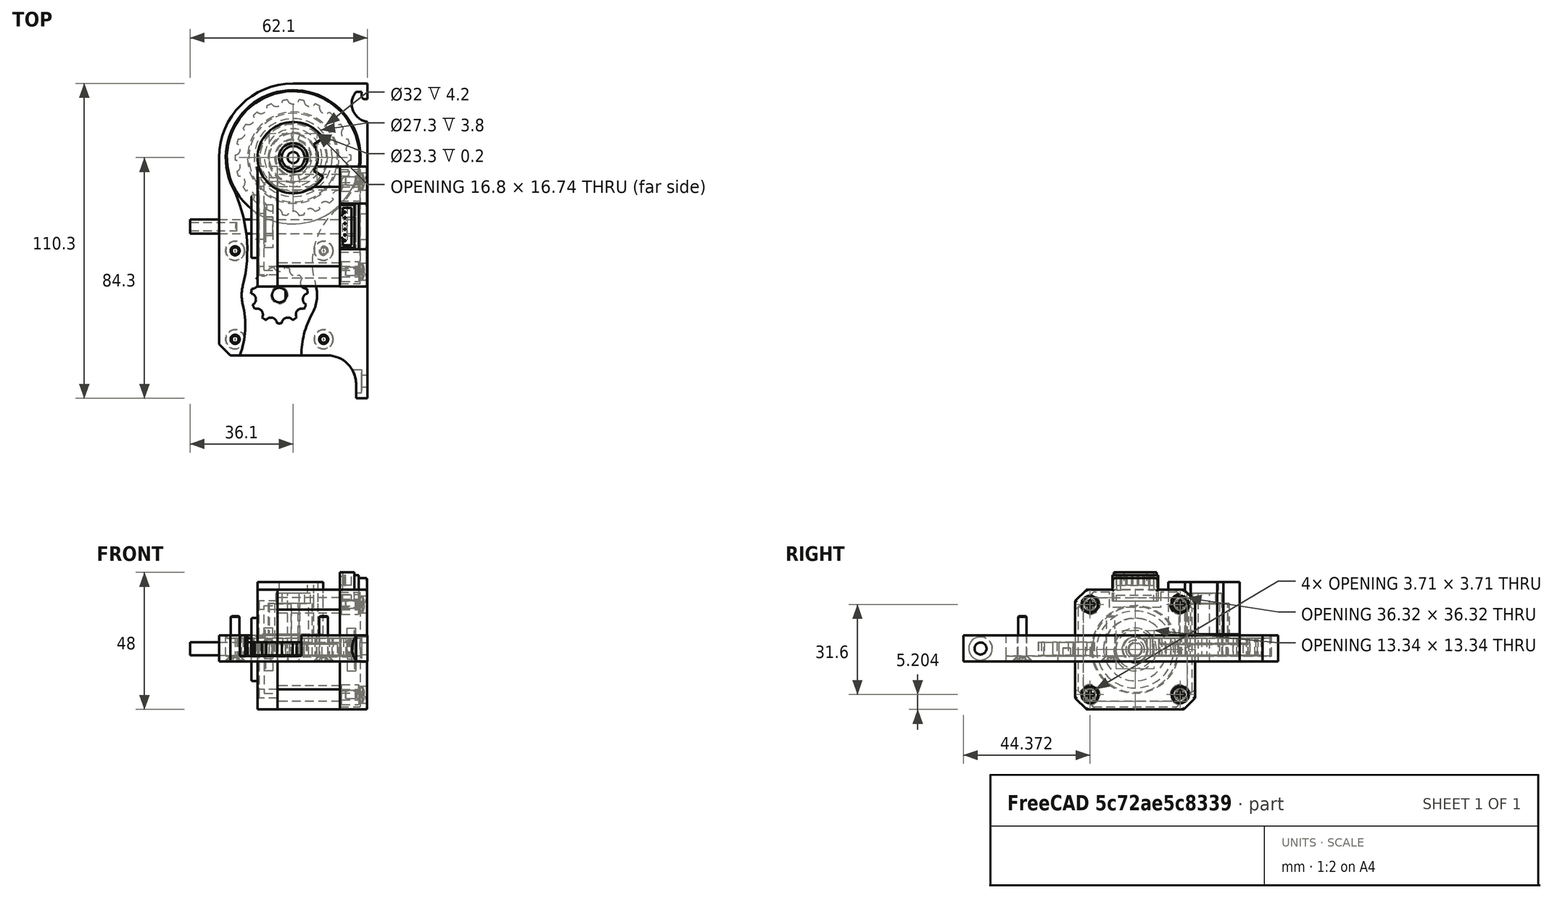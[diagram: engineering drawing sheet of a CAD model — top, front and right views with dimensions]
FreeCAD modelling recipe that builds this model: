
FCSTD DOCUMENT  (FreeCAD 0.19R24276 (Git))
Label: integrated-roller-clutch
License: All rights reserved
LicenseURL: http://en.wikipedia.org/wiki/All_rights_reserved
objects: Sketcher::SketchObject×27, Part::Feature×20, PartDesign::Pad×16, PartDesign::Pocket×11, PartDesign::Body×4, Part::FeaturePython×4, Spreadsheet::Sheet×2, PartDesign::PolarPattern×2, PartDesign::Hole×2, PartDesign::Chamfer×1, PartDesign::Fillet×1, Part::Compound2×1
note: 119 computed .brp shape members not serialized (recipe doc carries the construction recipe); baked Part::Feature solids carry a one-line shape summary decoded from their .brp

FEATURE [Spreadsheet::Sheet] Spreadsheet  label="Params"
  cells = A3=Chain Ball Spacing; B3(ChainBallSpacing)=5.95; A4=Chain Ball Diameter; B4(ChainBallDiameter)=4.2; A5=Chain String Diameter; B5(ChainStringDiameter)=1; A7=Cover Max Diameter; B7(CoverMaxDiameter)=46; A8=Cover Boom Diameter; B8(CoverBoomDiameter)=20; A11=Cover Pulley Teeths; B11(CoverPulleyTeeths)=22; A12=Motor Pulley Teeths; B12(MotorPulleyTeeths)=11
FEATURE [Sketcher::SketchObject] Sketch  label="Bracket Profile"
  FullyConstrained = false
  MapMode = 5
  Support = -> [XY_Plane]
  expr: Constraints[27] = <<Params>>.CoverBoomDiameter
  expr: Constraints[1] = <<Params>>.CoverMaxDiameter
  sketch-geometry (18):
    g0: Circle CenterX=0 CenterY=0 CenterZ=0 NormalX=0 NormalY=0 NormalZ=1 AngleXU=0 Radius=23
    g1: GeomPoint X=0 Y=23 Z=0
    g2: GeomPoint X=23 Y=0 Z=0
    g3: GeomPoint X=26 Y=26 Z=0
    g4: LineSegment StartX=26 StartY=26 StartZ=0 EndX=26 EndY=-84.3 EndZ=0
    g5: LineSegment StartX=26 StartY=-84.3 StartZ=0 EndX=22 EndY=-84.3 EndZ=0
    g6: LineSegment StartX=22 StartY=-84.3 StartZ=0 EndX=22 EndY=-79.3 EndZ=0
    g7: LineSegment StartX=12 StartY=-69.3 StartZ=0 EndX=-26 EndY=-69.3 EndZ=0
    g8: LineSegment StartX=-26 StartY=-69.3 StartZ=0 EndX=-26 EndY=26 EndZ=0
    g9: LineSegment StartX=-26 StartY=26 StartZ=0 EndX=26 EndY=26 EndZ=0
    g10: GeomPoint X=-23 Y=0 Z=0
    g11: GeomPoint X=0 Y=-23 Z=0
    g12: ArcOfCircle CenterX=12 CenterY=-79.3 CenterZ=0 NormalX=0 NormalY=0 NormalZ=1 AngleXU=0 Radius=10 StartAngle=0 EndAngle=1.5708
    g13: LineSegment StartX=16.3 StartY=-69.3 StartZ=0 EndX=16.3 EndY=-27 EndZ=0
    g14: LineSegment StartX=16.3 StartY=-27 StartZ=0 EndX=-26 EndY=-27 EndZ=0
    g15: LineSegment StartX=-26 StartY=-27 StartZ=0 EndX=-26 EndY=-69.3 EndZ=0
    g16: LineSegment StartX=-26 StartY=-69.3 StartZ=0 EndX=16.3 EndY=-69.3 EndZ=0
    g17: Circle CenterX=-4.85 CenterY=-48.15 CenterZ=0 NormalX=0 NormalY=0 NormalZ=1 AngleXU=0 Radius=29.9106
  constraints (46):
    c: Coincident(g0,g-1)
    c: Diameter(g0) = 46
    c: PointOnObject(g1,g-2)
    c: PointOnObject(g1,g0)
    c: PointOnObject(g2,g0)
    c: PointOnObject(g2,g-1)
    c: DistanceY(g1,g3) = 3
    c: DistanceX(g2,g3) = 3
    c: Coincident(g4,g3)
    c: Vertical(g4)
    c: Coincident(g4,g5)
    c: Horizontal(g5)
    c: Coincident(g5,g6)
    c: Vertical(g6)
    c: Coincident(g7,g8)
    c: Vertical(g8)
    c: Coincident(g8,g9)
    c: Coincident(g9,g3)
    c: Horizontal(g9)
    c: Horizontal(g7,g7)
    c: Distance(g5) = 4
    c: Distance(g6) = 5
    c: PointOnObject(g10,g0)
    c: PointOnObject(g11,g0)
    c: PointOnObject(g11,g-2)
    c: PointOnObject(g10,g-1)
    c: DistanceX(g8,g10) = 3
    c: Diameter(g12) = 20
    c: Angle(g12) = 1.5708
    c: Tangent(g12,g6) = -1.5708
    c: Coincident(g7,g12)
    c: Coincident(g13,g14)
    c: Coincident(g14,g15)
    c: Coincident(g15,g16)
    c: Coincident(g16,g13)
    c: Equal(g13,g14)
    c: Equal(g13,g15)
    c: Equal(g13,g16)
    c: PointOnObject(g13,g17)
    c: PointOnObject(g14,g17)
    c: PointOnObject(g15,g17)
    c: PointOnObject(g16,g17)
    c: Distance(g16) = 42.3
    c: Angle(g16) = 0
    c: Coincident(g15,g7)
    c: DistanceY(g13,g11) = 4
FEATURE [PartDesign::Pad] Pad  label="Bracket Body"
  AllowMultiFace = false
  Direction = (1,1,1)
  Length = 2
  Length2 = 100
  Profile = -> Sketch
  Type = 0
FEATURE [Sketcher::SketchObject] Sketch001  label="Bearing Cup Profile"
  FullyConstrained = true
  MapMode = 5
  Placement = pos=(0,0,2) rot=(0,0,1;0rad)
  Support = -> [Pad]
  expr: Constraints[0] = Spreadsheet001.MainCoverBearingOuterDiameter + 0.3
  expr: Constraints[1] = Spreadsheet001.MainCoverBearingOuterDiameter + 4
  sketch-geometry (2):
    g0: Circle CenterX=0 CenterY=0 CenterZ=0 NormalX=0 NormalY=0 NormalZ=1 AngleXU=0 Radius=13.65
    g1: Circle CenterX=0 CenterY=0 CenterZ=0 NormalX=0 NormalY=0 NormalZ=1 AngleXU=0 Radius=15.5
  constraints (4):
    c: Diameter(g0) = 27.3
    c: Diameter(g1) = 31
    c: Coincident(g1,g0)
    c: Coincident(g1,g-1)
FEATURE [PartDesign::Pad] Pad001  label="Main Bearing Cup"
  AllowMultiFace = false
  BaseFeature = -> Pad
  Direction = (1,1,1)
  Length = 4
  Length2 = 100
  Profile = -> Sketch001
  Type = 0
  expr: Length = Spreadsheet001.CoverBearingWidth
FEATURE [Sketcher::SketchObject] Sketch002  label="Bearing Shim Profile"
  ExternalGeometry = -> [Pad001]
  FullyConstrained = true
  MapMode = 5
  Placement = pos=(0,0,2) rot=(0,0,1;0rad)
  Support = -> [Pad001]
  sketch-geometry (4):
    g0: GeomPoint X=-13.65 Y=0 Z=0
    g1: GeomPoint X=-11.65 Y=0 Z=0
    g2: Circle CenterX=0 CenterY=0 CenterZ=0 NormalX=0 NormalY=0 NormalZ=1 AngleXU=0 Radius=11.65
    g3: Circle CenterX=0 CenterY=0 CenterZ=0 NormalX=0 NormalY=0 NormalZ=1 AngleXU=0 Radius=13.65
  constraints (8):
    c: PointOnObject(g0,g-1)
    c: PointOnObject(g0,g-3)
    c: PointOnObject(g1,g-1)
    c: Coincident(g2,g-1)
    c: PointOnObject(g1,g2)
    c: Coincident(g3,g2)
    c: PointOnObject(g0,g3)
    c: Distance(g0,g1) = 2
FEATURE [PartDesign::Pad] Pad002  label="Main Bearing Shim"
  AllowMultiFace = false
  BaseFeature = -> Pad001
  Direction = (1,1,1)
  Length = 0.2
  Length2 = 100
  Profile = -> Sketch002
  Type = 0
FEATURE [Sketcher::SketchObject] Sketch003  label="Spring Shim Profile"
  FullyConstrained = true
  MapMode = 5
  Placement = pos=(0,0,2) rot=(0,0,1;0rad)
  Support = -> [Pad002]
  sketch-geometry (1):
    g0: Circle CenterX=0 CenterY=0 CenterZ=0 NormalX=0 NormalY=0 NormalZ=1 AngleXU=0 Radius=6.1
  constraints (2):
    c: Coincident(g0,g-1)
    c: Diameter(g0) = 12.2
FEATURE [PartDesign::Pad] Pad003  label="Spring Shim"
  AllowMultiFace = false
  BaseFeature = -> Pad002
  Direction = (1,1,1)
  Length = 0.2
  Length2 = 100
  Profile = -> Sketch003
  Type = 0
FEATURE [Sketcher::SketchObject] Sketch004  label="Spring Stud Profile"
  FullyConstrained = true
  MapMode = 5
  Placement = pos=(0,0,2.2) rot=(0,0,1;0rad)
  Support = -> [Pad003]
  sketch-geometry (1):
    g0: Circle CenterX=0 CenterY=0 CenterZ=0 NormalX=0 NormalY=0 NormalZ=1 AngleXU=0 Radius=5.4
  constraints (2):
    c: Coincident(g0,g-1)
    c: Diameter(g0) = 10.8
FEATURE [PartDesign::Pad] Pad004  label="Spring Stud"
  AllowMultiFace = false
  BaseFeature = -> Pad003
  Direction = (1,1,1)
  Length = 18.2
  Length2 = 100
  Profile = -> Sketch004
  Type = 0
FEATURE [Sketcher::SketchObject] Sketch005  label="Adapter Bearing Profile"
  FullyConstrained = true
  MapMode = 5
  Placement = pos=(0,0,20.4) rot=(0,0,1;0rad)
  Support = -> [Pad004]
  expr: Constraints[1] = <<StockParts>>.AdapterBearingInnerDiameter
  sketch-geometry (1):
    g0: Circle CenterX=0 CenterY=0 CenterZ=0 NormalX=0 NormalY=0 NormalZ=1 AngleXU=0 Radius=4
  constraints (2):
    c: Coincident(g0,g-1)
    c: Diameter(g0) = 8
FEATURE [PartDesign::Pad] Pad005  label="Adapter Bearing Stud"
  AllowMultiFace = false
  BaseFeature = -> Pad004
  Direction = (1,1,1)
  Length = 3.5
  Length2 = 100
  Profile = -> Sketch005
  Type = 0
  expr: Length = <<StockParts>>.AdapterBearingWidth
FEATURE [Sketcher::SketchObject] Sketch006  label="Pulley Base Profile"
  FullyConstrained = false
  MapMode = 5
  Support = -> [XY_Plane001]
  expr: Constraints[0] = <<Params>>.CoverPulleyTeeths * <<Params>>.ChainBallSpacing / pi - <<Params>>.ChainStringDiameter
  sketch-geometry (1):
    g0: Circle CenterX=0 CenterY=0 CenterZ=0 NormalX=0 NormalY=0 NormalZ=1 AngleXU=0 Radius=20.3334
  constraints (2):
    c: Diameter(g0) = 40.6668
    c: Coincident(g0,g-1)
FEATURE [PartDesign::Pad] Pad006  label="Pulley Body"
  AllowMultiFace = false
  Direction = (1,1,1)
  Length = 6
  Length2 = 100
  Profile = -> Sketch006
  Type = 0
FEATURE [Sketcher::SketchObject] Sketch007  label="Chain Ball Profile"
  FullyConstrained = false
  MapMode = 5
  Placement = pos=(0,0,6) rot=(0,0,1;0rad)
  Support = -> [Pad006]
  expr: Constraints[1] = <<Params>>.CoverPulleyTeeths * <<Params>>.ChainBallSpacing / pi / 2
  expr: Constraints[2] = <<Params>>.ChainBallDiameter
  sketch-geometry (1):
    g0: Circle CenterX=0 CenterY=20.8334 CenterZ=0 NormalX=0 NormalY=0 NormalZ=1 AngleXU=0 Radius=2.1
  constraints (3):
    c: PointOnObject(g0,g-2)
    c: Distance(g-1,g0) = 20.8334
    c: Diameter(g0) = 4.2
FEATURE [PartDesign::Pocket] Pocket  label="Single Teeth Cutout"
  AllowMultiFace = false
  BaseFeature = -> Pad006
  Length = 5
  Length2 = 100
  Profile = -> Sketch007
  Type = 1
FEATURE [PartDesign::PolarPattern] PolarPattern  label="All Teeth Cutout"
  Angle = 360
  Axis = -> Sketch007 [N_Axis]
  BaseFeature = -> Pocket
  Occurrences = 22
  Originals = -> [Pocket]
  expr: Occurrences = <<Params>>.CoverPulleyTeeths
FEATURE [Sketcher::SketchObject] Sketch008  label="Bearing Profile"
  FullyConstrained = true
  MapMode = 5
  Placement = pos=(0,0,0) rot=(1,0,0;3.14159rad)
  Support = -> [PolarPattern]
  expr: Constraints[3] = <<StockParts>>.MainCoverBearingInnerDiameter + 0.15
  expr: Constraints[1] = <<StockParts>>.MainCoverBearingOuterDiameter + 4 + 1
  sketch-geometry (2):
    g0: Circle CenterX=0 CenterY=0 CenterZ=0 NormalX=0 NormalY=0 NormalZ=1 AngleXU=0 Radius=16
    g1: Circle CenterX=0 CenterY=0 CenterZ=0 NormalX=0 NormalY=0 NormalZ=1 AngleXU=0 Radius=10.075
  constraints (4):
    c: Coincident(g0,g-1)
    c: Diameter(g0) = 32
    c: Coincident(g1,g0)
    c: Diameter(g1) = 20.15
FEATURE [Spreadsheet::Sheet] Spreadsheet001  label="StockParts"
  cells = A5=Cover Bearing Width; B5(CoverBearingWidth)=4; A6=Cover Outer Diameter; B6(MainCoverBearingOuterDiameter)=27; A7=Cover Inner Diameter; B7(MainCoverBearingInnerDiameter)=20; A10=Adapter Bearing Width; B10(AdapterBearingWidth)=3.5; A11=Adapter Bearing Outer Diameter; B11(AdapterBearingOuterDiameter)=12; A12=Adapter Bearing Inner Diameter; B12(AdapterBearingInnerDiameter)=8
FEATURE [Sketcher::SketchObject] Sketch013
  FullyConstrained = false
  MapMode = 5
  Placement = pos=(0,0,6) rot=(0,0,1;0rad)
  Support = -> [PolarPattern]
  expr: Constraints[1] = <<Params>>.ChainBallSpacing * <<Params>>.CoverPulleyTeeths / pi + <<Params>>.ChainBallDiameter + 1 - 0.4
  sketch-geometry (1):
    g0: Circle CenterX=0 CenterY=0 CenterZ=0 NormalX=0 NormalY=0 NormalZ=1 AngleXU=0 Radius=23.2334
  constraints (2):
    c: Coincident(g0,g-1)
    c: Diameter(g0) = 46.4668
FEATURE [PartDesign::Pad] Pad007
  AllowMultiFace = false
  BaseFeature = -> PolarPattern
  Direction = (1,1,1)
  Length = 1
  Length2 = 100
  Profile = -> Sketch013
  Type = 0
FEATURE [PartDesign::Pocket] Pocket001
  AllowMultiFace = false
  BaseFeature = -> Pad007
  Length = 4.2
  Length2 = 100
  Profile = -> Sketch008
  Type = 0
  expr: Length = Spreadsheet001.CoverBearingWidth + 0.2
FEATURE [Sketcher::SketchObject] Sketch014
  FullyConstrained = true
  MapMode = 5
  Placement = pos=(0,0,4.2) rot=(1,0,0;3.14159rad)
  Support = -> [Pocket001]
  expr: Constraints[1] = <<StockParts>>.MainCoverBearingInnerDiameter + 4
  sketch-geometry (1):
    g0: Circle CenterX=0 CenterY=0 CenterZ=0 NormalX=0 NormalY=0 NormalZ=1 AngleXU=0 Radius=12
  constraints (2):
    c: Coincident(g0,g-1)
    c: Diameter(g0) = 24
FEATURE [PartDesign::Pad] Pad008
  AllowMultiFace = false
  BaseFeature = -> Pocket001
  Direction = (1,1,1)
  Length = 0.2
  Length2 = 100
  Profile = -> Sketch014
  Type = 0
FEATURE [Sketcher::SketchObject] Sketch015
  FullyConstrained = true
  MapMode = 5
  Placement = pos=(0,0,0) rot=(1,0,0;3.14159rad)
  Support = -> [Pad008]
  sketch-geometry (1):
    g0: Circle CenterX=0 CenterY=0 CenterZ=0 NormalX=0 NormalY=0 NormalZ=1 AngleXU=0 Radius=8.4
  constraints (2):
    c: Coincident(g0,g-1)
    c: Diameter(g0) = 16.8
FEATURE [PartDesign::Pocket] Pocket002
  AllowMultiFace = false
  BaseFeature = -> Pad008
  Length = 5
  Length2 = 100
  Profile = -> Sketch015
  Type = 1
FEATURE [Sketcher::SketchObject] Sketch016
  ExternalGeometry = -> [Pocket002]
  FullyConstrained = true
  MapMode = 5
  Placement = pos=(0,0,0) rot=(1,0,0;3.14159rad)
  Support = -> [Pocket002]
  sketch-geometry (7):
    g0: GeomPoint X=8.4 Y=0 Z=0
    g1: LineSegment StartX=-0.732108 StartY=-8.36804 StartZ=0 EndX=-0.566512 EndY=-6.47527 EndZ=0
    g2: LineSegment StartX=-0.732108 StartY=8.36804 StartZ=0 EndX=-0.566512 EndY=6.47527 EndZ=0
    g3: LineSegment StartX=-0.732108 StartY=8.36804 StartZ=0 EndX=8.4 EndY=0 EndZ=0
    g4: LineSegment StartX=8.4 StartY=0 StartZ=0 EndX=-0.732108 EndY=-8.36804 EndZ=0
    g5: ArcOfCircle CenterX=0 CenterY=0 CenterZ=0 NormalX=0 NormalY=0 NormalZ=1 AngleXU=0 Radius=8.4 StartAngle=1.65806 EndAngle=4.62512
    g6: ArcOfCircle CenterX=0 CenterY=0 CenterZ=0 NormalX=0 NormalY=0 NormalZ=1 AngleXU=0 Radius=6.5 StartAngle=1.65806 EndAngle=4.62512
  constraints (18):
    c: PointOnObject(g0,g-1)
    c: PointOnObject(g1,g-3)
    c: Coincident(g3,g2)
    c: Coincident(g3,g0)
    c: Coincident(g4,g0)
    c: Coincident(g4,g1)
    c: Equal(g4,g3)
    c: Coincident(g5,g-1)
    c: Coincident(g5,g2)
    c: Coincident(g5,g1)
    c: Coincident(g6,g5)
    c: Coincident(g6,g1)
    c: Coincident(g6,g2)
    c: Perpendicular(g6,g2)
    c: Perpendicular(g5,g1)
    c: Diameter(g6) = 13
    c: Angle(g6) = 2.96706
    c: PointOnObject(g0,g-3)
FEATURE [PartDesign::Pad] Pad009
  AllowMultiFace = false
  BaseFeature = -> Pocket002
  Direction = (1,1,1)
  Length = 18
  Length2 = 100
  Profile = -> Sketch016
  Reversed = true
  Type = 0
FEATURE [PartDesign::Body] Body001  label="Cover Pulley"
  Group = -> [Sketch006,Pad006,Sketch007,Pocket,PolarPattern,Sketch008,Sketch013,Pad007,Pocket001,Sketch014,Pad008,Sketch015,Pocket002,Sketch016,Pad009]
  Origin = -> Origin001
  Placement = pos=(0,0,2.2) rot=(0,0,1;0rad)
  Tip = -> Pad009
FEATURE [Sketcher::SketchObject] Sketch024
  FullyConstrained = false
  MapMode = 5
  Support = -> [XY_Plane004]
  expr: Constraints[1] = <<Params>>.ChainBallSpacing * <<Params>>.MotorPulleyTeeths / pi - <<Params>>.ChainStringDiameter
  sketch-geometry (1):
    g0: Circle CenterX=0 CenterY=0 CenterZ=0 NormalX=0 NormalY=0 NormalZ=1 AngleXU=0 Radius=9.91669
  constraints (2):
    c: Coincident(g0,g-1)
    c: Diameter(g0) = 19.8334
FEATURE [PartDesign::Pad] Pad016
  AllowMultiFace = false
  Direction = (1,1,1)
  Length = 4.6
  Length2 = 100
  Profile = -> Sketch024
  Type = 0
FEATURE [Sketcher::SketchObject] Sketch025
  FullyConstrained = false
  MapMode = 5
  Placement = pos=(0,0,4.6) rot=(0,0,1;0rad)
  Support = -> [Pad016]
  expr: Constraints[1] = <<Params>>.ChainBallDiameter
  expr: Constraints[2] = <<Params>>.ChainBallSpacing * <<Params>>.MotorPulleyTeeths / pi / 2
  sketch-geometry (1):
    g0: Circle CenterX=0 CenterY=10.4167 CenterZ=0 NormalX=0 NormalY=0 NormalZ=1 AngleXU=0 Radius=2.1
  constraints (3):
    c: PointOnObject(g0,g-2)
    c: Diameter(g0) = 4.2
    c: Distance(g-1,g0) = 10.4167
FEATURE [PartDesign::Pocket] Pocket004
  AllowMultiFace = false
  BaseFeature = -> Pad016
  Length = 5
  Length2 = 100
  Profile = -> Sketch025
  Type = 1
FEATURE [PartDesign::PolarPattern] PolarPattern001
  Angle = 360
  Axis = -> Sketch025 [N_Axis]
  BaseFeature = -> Pocket004
  Occurrences = 11
  Originals = -> [Pocket004]
  expr: Occurrences = <<Params>>.MotorPulleyTeeths
FEATURE [Sketcher::SketchObject] Sketch026
  FullyConstrained = false
  MapMode = 5
  Placement = pos=(0,0,4.6) rot=(0,0,1;0rad)
  Support = -> [PolarPattern001]
  sketch-geometry (2):
    g0: ArcOfCircle CenterX=0 CenterY=0 CenterZ=0 NormalX=0 NormalY=0 NormalZ=1 AngleXU=0 Radius=2.55 StartAngle=0.567705 EndAngle=5.71548
    g1: LineSegment StartX=2.15 StartY=-1.37113 StartZ=0 EndX=2.15 EndY=1.37113 EndZ=0
  constraints (6):
    c: Coincident(g0,g-1)
    c: Vertical(g0,g0)
    c: Coincident(g1,g0)
    c: Coincident(g1,g0)
    c: DistanceX(g0,g0) = 2.15
    c: Diameter(g0) = 5.1
FEATURE [PartDesign::Pocket] Pocket005
  AllowMultiFace = false
  BaseFeature = -> PolarPattern001
  Length = 5
  Length2 = 100
  Profile = -> Sketch026
  Type = 1
FEATURE [PartDesign::Pad] Pad018  label="Chain Compartment"
  AllowMultiFace = false
  BaseFeature = -> Pad005
  Direction = (1,1,1)
  Length = 7.2
  Length2 = 100
  Profile = -> Pad005 [Face5]
  Type = 0
FEATURE [Sketcher::SketchObject] Sketch034
  ExternalGeometry = -> [Pad018]
  FullyConstrained = true
  MapMode = 5
  Placement = pos=(0,0,9.2) rot=(0,0,1;0rad)
  Support = -> [Pad018]
  sketch-geometry (1):
    g0: Circle CenterX=-4.85 CenterY=-48.15 CenterZ=0 NormalX=0 NormalY=0 NormalZ=1 AngleXU=0 Radius=3
  constraints (3):
    c: Diameter(g0) = 6
    c: DistanceX(g-3,g0) = 21.15
    c: DistanceY(g-3,g0) = 21.15
FEATURE [PartDesign::Pocket] Pocket010  label="Shaft Hole"
  AllowMultiFace = false
  BaseFeature = -> Pad018
  Length = 5
  Length2 = 100
  Profile = -> Sketch034
  Type = 1
FEATURE [Sketcher::SketchObject] Sketch035
  ExternalGeometry = -> [Pocket010]
  FullyConstrained = true
  MapMode = 5
  Placement = pos=(0,0,0) rot=(1,0,0;3.14159rad)
  Support = -> [Pocket010]
  sketch-geometry (9):
    g0: LineSegment StartX=10.65 StartY=32.65 StartZ=0 EndX=10.65 EndY=63.65 EndZ=0
    g1: LineSegment StartX=10.65 StartY=63.65 StartZ=0 EndX=-20.35 EndY=63.65 EndZ=0
    g2: LineSegment StartX=-20.35 StartY=63.65 StartZ=0 EndX=-20.35 EndY=32.65 EndZ=0
    g3: LineSegment StartX=-20.35 StartY=32.65 StartZ=0 EndX=10.65 EndY=32.65 EndZ=0
    g4: Circle CenterX=-4.85 CenterY=48.15 CenterZ=0 NormalX=0 NormalY=0 NormalZ=1 AngleXU=0 Radius=21.9203
    g5: Circle CenterX=-20.35 CenterY=63.65 CenterZ=0 NormalX=0 NormalY=0 NormalZ=1 AngleXU=0 Radius=1.6
    g6: Circle CenterX=-20.35 CenterY=32.65 CenterZ=0 NormalX=0 NormalY=0 NormalZ=1 AngleXU=0 Radius=1.6
    g7: Circle CenterX=10.65 CenterY=32.65 CenterZ=0 NormalX=0 NormalY=0 NormalZ=1 AngleXU=0 Radius=1.6
    g8: Circle CenterX=10.65 CenterY=63.65 CenterZ=0 NormalX=0 NormalY=0 NormalZ=1 AngleXU=0 Radius=1.6
  constraints (22):
    c: Coincident(g0,g1)
    c: Coincident(g1,g2)
    c: Coincident(g2,g3)
    c: Coincident(g3,g0)
    c: Equal(g0,g1)
    c: Equal(g0,g2)
    c: Equal(g0,g3)
    c: PointOnObject(g0,g4)
    c: PointOnObject(g1,g4)
    c: PointOnObject(g2,g4)
    c: PointOnObject(g3,g4)
    c: Coincident(g4,g-3)
    c: Distance(g0) = 31
    c: Angle(g-1,g3) = 0
    c: Coincident(g5,g1)
    c: Coincident(g6,g2)
    c: Coincident(g7,g0)
    c: Coincident(g8,g0)
    c: Equal(g8,g5)
    c: Equal(g5,g6)
    c: Equal(g6,g7)
    c: Diameter(g8) = 3.2
FEATURE [PartDesign::Hole] Hole  label="Motor Mounting Screws"
  AllowMultiFace = false
  BaseFeature = -> Pocket010
  Depth = 25
  DepthType = 0
  Diameter = 3.2
  DrillForDepth = false
  DrillPoint = 1
  DrillPointAngle = 118
  HoleCutCountersinkAngle = 90
  HoleCutCustomValues = false
  HoleCutDepth = 0
  HoleCutDiameter = 6.8
  HoleCutType = 2
  ModelActualThread = false
  Profile = -> Sketch035
  Tapered = false
  TaperedAngle = 90
  ThreadAngle = 0
  ThreadClass = 0
  ThreadCutOffInner = 0
  ThreadCutOffOuter = 0
  ThreadDirection = 0
  ThreadFit = 0
  ThreadPitch = 0
  ThreadSize = 0
  ThreadType = 0
  Threaded = false
FEATURE [Sketcher::SketchObject] Sketch036
  ExternalGeometry = -> [Hole]
  FullyConstrained = true
  MapMode = 5
  Placement = pos=(0,0,9.2) rot=(0,0,1;0rad)
  Support = -> [Hole]
  expr: Constraints[16] = <<Params>>.ChainBallSpacing * <<Params>>.MotorPulleyTeeths / pi + <<Params>>.ChainBallDiameter + 1.4
  expr: Constraints[25] = <<Params>>.ChainBallSpacing * <<Params>>.CoverPulleyTeeths / pi + <<Params>>.ChainBallDiameter + 1.4
  sketch-geometry (11):
    g0: Circle CenterX=0 CenterY=0 CenterZ=0 NormalX=0 NormalY=0 NormalZ=1 AngleXU=0 Radius=15.5
    g1: ArcOfCircle CenterX=-66.09 CenterY=-32.4652 CenterZ=0 NormalX=0 NormalY=0 NormalZ=1 AngleXU=0 Radius=50 StartAngle=6.03245 EndAngle=6.73979
    g2: ArcOfCircle CenterX=31.6746 CenterY=-36.9043 CenterZ=0 NormalX=0 NormalY=0 NormalZ=1 AngleXU=0 Radius=25 StartAngle=2.28008 EndAngle=3.44028
    g3: GeomPoint X=-18.7 Y=-69.3 Z=0
    g4: GeomPoint X=7 Y=-69.3 Z=0
    g5: ArcOfCircle CenterX=-46.7615 CenterY=-58.6909 CenterZ=0 NormalX=0 NormalY=0 NormalZ=1 AngleXU=0 Radius=30 StartAngle=5.92173 EndAngle=6.52958
    g6: ArcOfCircle CenterX=32.8377 CenterY=-69.3 CenterZ=0 NormalX=0 NormalY=0 NormalZ=1 AngleXU=0 Radius=30 StartAngle=2.6302 EndAngle=3.14159
    g7: LineSegment StartX=-18.7 StartY=-69.3 StartZ=0 EndX=2.83766 EndY=-69.3 EndZ=0
    g8: ArcOfCircle CenterX=-4.85 CenterY=-48.15 CenterZ=0 NormalX=0 NormalY=0 NormalZ=1 AngleXU=0 Radius=13.2167 StartAngle=2.89086 EndAngle=3.38799
    g9: ArcOfCircle CenterX=-4.85 CenterY=-48.15 CenterZ=0 NormalX=0 NormalY=0 NormalZ=1 AngleXU=0 Radius=13.2167 StartAngle=5.77179 EndAngle=6.58187
    g10: ArcOfCircle CenterX=0 CenterY=0 CenterZ=0 NormalX=0 NormalY=0 NormalZ=1 AngleXU=0 Radius=23.6334 StartAngle=5.42168 EndAngle=9.88138
  constraints (27):
    c: Equal(g0,g-3)
    c: Coincident(g0,g-1)
    c: Radius(g2) = 25
    c: Radius(g1) = 50
    c: PointOnObject(g3,g-5)
    c: PointOnObject(g4,g-5)
    c: Distance(g3,g-5) = 7.3
    c: Distance(g4,g-5) = 5
    c: PointOnObject(g6,g-5)
    c: Perpendicular(g6,g-5)
    c: Radius(g5) = 30
    c: Radius(g6) = 30
    c: Coincident(g7,g5)
    c: Coincident(g7,g6)
    c: Coincident(g3,g5)
    c: Coincident(g9,g8)
    c: Diameter(g9) = 26.4334
    c: Equal(g9,g8)
    c: Tangent(g9,g6) = 1.5708
    c: Tangent(g9,g2) = 1.5708
    c: Tangent(g5,g8) = 1.5708
    c: Tangent(g8,g1) = 1.5708
    c: Coincident(g10,g0)
    c: Tangent(g1,g10) = 1.5708
    c: Tangent(g2,g10) = 1.5708
    c: Diameter(g10) = 47.2668
    c: Coincident(g-4,g8)
FEATURE [PartDesign::Pocket] Pocket011  label="Chain Guide"
  AllowMultiFace = false
  BaseFeature = -> Hole
  Length = 0
  Length2 = 100
  Profile = -> Sketch036
  Type = 3
  UpToFace = -> Hole [Face31]
FEATURE [Sketcher::SketchObject] Sketch037
  ExternalGeometry = -> [Pocket005]
  FullyConstrained = false
  MapMode = 5
  Placement = pos=(0,0,4.6) rot=(0,0,1;0rad)
  Support = -> [Pocket005]
  sketch-geometry (1):
    g0: Circle CenterX=0 CenterY=0 CenterZ=0 NormalX=0 NormalY=0 NormalZ=1 AngleXU=0 Radius=2.55
  constraints (2):
    c: Coincident(g0,g-1)
    c: Equal(g0,g-3)
FEATURE [PartDesign::Pocket] Pocket012
  AllowMultiFace = false
  BaseFeature = -> Pocket005
  Length = 2
  Length2 = 100
  Profile = -> Sketch037
  Type = 0
FEATURE [PartDesign::Body] Body004  label="Motor Pulley"
  Group = -> [Sketch024,Pad016,Sketch025,Pocket004,PolarPattern001,Sketch026,Pocket005,Sketch037,Pocket012]
  Origin = -> Origin004
  Placement = pos=(-4.85,-48.15,2.2) rot=(0,0,1;0rad)
  Tip = -> Pocket012
FEATURE [PartDesign::Chamfer] Chamfer001
  Angle = 45
  Base = -> Pocket011 [Edge23,Edge62]
  BaseFeature = -> Pocket011
  ChamferType = 0
  FlipDirection = false
  Size = 4
  Size2 = 1
  SupportTransform = false
FEATURE [Sketcher::SketchObject] Sketch039
  FullyConstrained = false
  MapMode = 5
  Placement = pos=(22,0,0) rot=(0.57735,-0.57735,-0.57735;2.0944rad)
  sketch-geometry (3):
    g0: Circle CenterX=78.3 CenterY=4.6 CenterZ=0 NormalX=0 NormalY=0 NormalZ=1 AngleXU=0 Radius=4.1
    g1: LineSegment StartX=78.3 StartY=4.6 StartZ=0 EndX=84.3 EndY=9.2 EndZ=0
    g2: LineSegment StartX=78.3 StartY=4.6 StartZ=0 EndX=84.3 EndY=0 EndZ=0
  constraints (5):
    c: Coincident(g1,g0)
    c: Coincident(g2,g0)
    c: Equal(g2,g1)
    c: DistanceX(g0,g1) = 6
    c: Diameter(g0) = 8.2
FEATURE [PartDesign::Hole] Hole001
  AllowMultiFace = false
  BaseFeature = -> Chamfer001
  Depth = 25
  DepthType = 1
  Diameter = 4.2
  DrillForDepth = false
  DrillPoint = 1
  DrillPointAngle = 118
  HoleCutCountersinkAngle = 90
  HoleCutCustomValues = false
  HoleCutDepth = 2
  HoleCutDiameter = 8.2
  HoleCutType = 1
  ModelActualThread = false
  Profile = -> Sketch039
  Tapered = false
  TaperedAngle = 90
  ThreadAngle = 0
  ThreadClass = 0
  ThreadCutOffInner = 0
  ThreadCutOffOuter = 0
  ThreadDirection = 0
  ThreadFit = 0
  ThreadPitch = 0
  ThreadSize = 0
  ThreadType = 0
  Threaded = false
FEATURE [PartDesign::Pocket] Pocket014
  AllowMultiFace = false
  BaseFeature = -> Hole001
  Length = 2
  Length2 = 100
  Profile = -> Sketch039
  Reversed = true
  Type = 0
FEATURE [Sketcher::SketchObject] Sketch040
  FullyConstrained = true
  MapMode = 5
  Placement = pos=(0,0,23.9) rot=(0,0,1;0rad)
  Support = -> [Pad005]
  sketch-geometry (1):
    g0: Circle CenterX=0 CenterY=0 CenterZ=0 NormalX=0 NormalY=0 NormalZ=1 AngleXU=0 Radius=1.95
  constraints (2):
    c: Coincident(g0,g-1)
    c: Diameter(g0) = 3.9
FEATURE [PartDesign::Pocket] Pocket020
  AllowMultiFace = false
  BaseFeature = -> Pocket014
  Length = 5
  Length2 = 100
  Profile = -> Sketch040
  Type = 1
FEATURE [PartDesign::Fillet] Fillet
  Base = -> Pocket020 [Edge48,Edge16]
  BaseFeature = -> Pocket020
  Radius = 26
  SupportTransform = false
  expr: Radius = <<Params>>.CoverMaxDiameter / 2 + 3
FEATURE [Sketcher::SketchObject] Sketch048
  ExternalGeometry = -> [Fillet]
  FullyConstrained = true
  MapMode = 5
  Placement = pos=(0,0,9.2) rot=(0,0,1;0rad)
  Support = -> [Fillet]
  sketch-geometry (7):
    g0: LineSegment StartX=26 StartY=20.5 StartZ=0 EndX=25 EndY=20.5 EndZ=0
    g1: LineSegment StartX=24 StartY=21.5 StartZ=0 EndX=24 EndY=23 EndZ=0
    g2: LineSegment StartX=24 StartY=23 StartZ=0 EndX=22 EndY=23 EndZ=0
    g3: LineSegment StartX=26 StartY=12.5 StartZ=0 EndX=26 EndY=20.5 EndZ=0
    g4: ArcOfCircle CenterX=25 CenterY=21.5 CenterZ=0 NormalX=0 NormalY=0 NormalZ=1 AngleXU=0 Radius=1 StartAngle=3.14159 EndAngle=4.71239
    g5: GeomPoint X=20.5 Y=18.9 Z=0
    g6: ArcOfCircle CenterX=26.9377 CenterY=18.8691 CenterZ=0 NormalX=0 NormalY=0 NormalZ=1 AngleXU=0 Radius=6.43779 StartAngle=2.44493 EndAngle=4.56621
  constraints (20):
    c: PointOnObject(g0,g-3)
    c: Horizontal(g0)
    c: Vertical(g1)
    c: Coincident(g1,g2)
    c: Horizontal(g2)
    c: PointOnObject(g3,g-3)
    c: Coincident(g3,g0)
    c: DistanceX(g1,g-3) = 2
    c: DistanceY(g1,g-3) = 3
    c: Distance(g0,g3) = 8
    c: DistanceX(g2,g1) = 2
    c: Tangent(g1,g4) = 1.5708
    c: Tangent(g0,g4) = 1.5708
    c: Radius(g4) = 1
    c: DistanceY(g0,g1) = 2.5
    c: DistanceY(g5,g2) = 4.1
    c: DistanceX(g5,g1) = 3.5
    c: Coincident(g6,g2)
    c: Coincident(g6,g3)
    c: PointOnObject(g5,g6)
FEATURE [PartDesign::Pocket] Pocket021
  AllowMultiFace = false
  BaseFeature = -> Fillet
  Length = 5
  Length2 = 100
  Profile = -> Sketch048
  Type = 1
FEATURE [PartDesign::Body] Body  label="Back Bracket"
  Group = -> [Sketch,Pad,Sketch001,Pad001,Sketch002,Pad002,Sketch003,Pad003,Sketch004,Pad004,Sketch005,Pad005,Pad018,Sketch034,Pocket010,Sketch035,Hole,Sketch036,Pocket011,Chamfer001,Sketch039,Hole001,Pocket014,Sketch040,Pocket020,Fillet,Sketch048,Pocket021]
  Origin = -> Origin
  Tip = -> Pocket021
FEATURE [Sketcher::SketchObject] Sketch049
  FullyConstrained = false
  MapMode = 5
  Support = -> [XY_Plane007]
  sketch-geometry (7):
    g0: ArcOfCircle CenterX=0 CenterY=0 CenterZ=0 NormalX=0 NormalY=0 NormalZ=1 AngleXU=0 Radius=8.1 StartAngle=4.99164 EndAngle=7.57473
    g1: ArcOfCircle CenterX=0 CenterY=0 CenterZ=0 NormalX=0 NormalY=0 NormalZ=1 AngleXU=0 Radius=6.5 StartAngle=4.99164 EndAngle=7.57473
    g2: LineSegment StartX=1.79164 StartY=6.2482 StartZ=0 EndX=2.23266 EndY=7.78622 EndZ=0
    g3: LineSegment StartX=1.79164 StartY=-6.2482 StartZ=0 EndX=2.23266 EndY=-7.78622 EndZ=0
    g4: GeomPoint X=-5 Y=0 Z=0
    g5: LineSegment StartX=-5 StartY=0 StartZ=0 EndX=1.79164 EndY=6.2482 EndZ=0
    g6: LineSegment StartX=-5 StartY=0 StartZ=0 EndX=1.79164 EndY=-6.2482 EndZ=0
  constraints (18):
    c: Coincident(g0,g-1)
    c: Coincident(g1,g0)
    c: Coincident(g2,g1)
    c: Coincident(g2,g0)
    c: Coincident(g3,g1)
    c: Coincident(g3,g0)
    c: Perpendicular(g0,g2)
    c: Perpendicular(g1,g3)
    c: Diameter(g1) = 13
    c: Angle(g3,g2) = 2.58309
    c: PointOnObject(g4,g-1)
    c: Coincident(g5,g4)
    c: Coincident(g5,g1)
    c: Coincident(g6,g4)
    c: Coincident(g6,g1)
    c: Equal(g6,g5)
    c: Distance(g4,g0) = 5
    c: Distance(g2) = 1.6
FEATURE [PartDesign::Pad] Pad021
  AllowMultiFace = false
  Direction = (1,1,1)
  Length = 7.4
  Length2 = 100
  Profile = -> Sketch049
  Type = 0
FEATURE [Sketcher::SketchObject] Sketch050
  ExternalGeometry = -> [Pad021]
  FullyConstrained = true
  MapMode = 5
  Placement = pos=(0,0,7.4) rot=(0,0,1;0rad)
  Support = -> [Pad021]
  sketch-geometry (11):
    g0: ArcOfCircle CenterX=0 CenterY=0 CenterZ=0 NormalX=0 NormalY=0 NormalZ=1 AngleXU=0 Radius=8.8 StartAngle=1.29154 EndAngle=4.99164
    g1: LineSegment StartX=1.79164 StartY=6.2482 StartZ=0 EndX=2.42561 EndY=8.4591 EndZ=0
    g2: LineSegment StartX=1.79164 StartY=-6.2482 StartZ=0 EndX=2.42561 EndY=-8.4591 EndZ=0
    g3: ArcOfCircle CenterX=0 CenterY=0 CenterZ=0 NormalX=0 NormalY=0 NormalZ=1 AngleXU=0 Radius=6.5 StartAngle=4.99164 EndAngle=7.57473
    g4: ArcOfCircle CenterX=0 CenterY=0 CenterZ=0 NormalX=0 NormalY=0 NormalZ=1 AngleXU=0 Radius=12.5 StartAngle=0.567232 EndAngle=5.71595
    g5: LineSegment StartX=10.5424 StartY=6.71625 StartZ=0 EndX=7.25317 EndY=4.62078 EndZ=0
    g6: LineSegment StartX=10.5424 StartY=-6.71625 StartZ=0 EndX=7.25317 EndY=-4.62078 EndZ=0
    g7: ArcOfCircle CenterX=0 CenterY=0 CenterZ=0 NormalX=0 NormalY=0 NormalZ=1 AngleXU=0 Radius=8.6 StartAngle=5.71595 EndAngle=6.85042
    g8: GeomPoint X=15 Y=0 Z=0
    g9: LineSegment StartX=10.5424 StartY=6.71625 StartZ=0 EndX=15 EndY=0 EndZ=0
    g10: LineSegment StartX=15 StartY=0 StartZ=0 EndX=10.5424 EndY=-6.71625 EndZ=0
  constraints (29):
    c: Coincident(g0,g-1)
    c: Diameter(g0) = 17.6
    c: Coincident(g1,g-4)
    c: PointOnObject(g-4,g1)
    c: Coincident(g1,g0)
    c: Coincident(g2,g-5)
    c: Coincident(g2,g0)
    c: PointOnObject(g-5,g2)
    c: Coincident(g3,g0)
    c: Coincident(g3,g1)
    c: Coincident(g3,g2)
    c: Coincident(g4,g0)
    c: Coincident(g5,g4)
    c: Coincident(g6,g4)
    c: Coincident(g7,g0)
    c: Coincident(g7,g6)
    c: Coincident(g7,g5)
    c: Perpendicular(g4,g5)
    c: Perpendicular(g7,g6)
    c: Diameter(g4) = 25
    c: Diameter(g7) = 17.2
    c: Angle(g6,g5) = 1.13446
    c: PointOnObject(g8,g-1)
    c: Coincident(g9,g4)
    c: Coincident(g9,g8)
    c: Coincident(g10,g8)
    c: Coincident(g10,g4)
    c: Equal(g10,g9)
    c: Distance(g8,g0) = 15
FEATURE [PartDesign::Pad] Pad022
  AllowMultiFace = false
  BaseFeature = -> Pad021
  Direction = (1,1,1)
  Length = 10.8
  Length2 = 100
  Profile = -> Sketch050
  Type = 0
FEATURE [Sketcher::SketchObject] Sketch051
  ExternalGeometry = -> [Pad021]
  FullyConstrained = true
  MapMode = 5
  Placement = pos=(0,0,18.2) rot=(0,0,1;0rad)
  Support = -> [Pad022]
  expr: Constraints[0] = <<StockParts>>.AdapterBearingOuterDiameter + 0.2
  expr: Constraints[23] = Sketch050.Constraints[21]
  expr: Constraints[3] = Sketch050.Constraints[1]
  expr: Constraints[22] = Sketch050.Constraints[20]
  expr: Constraints[21] = Sketch050.Constraints[19]
  expr: Constraints[30] = Sketch050.Constraints[28]
  sketch-geometry (12):
    g0: Circle CenterX=0 CenterY=0 CenterZ=0 NormalX=0 NormalY=0 NormalZ=1 AngleXU=0 Radius=6.1
    g1: ArcOfCircle CenterX=0 CenterY=0 CenterZ=0 NormalX=0 NormalY=0 NormalZ=1 AngleXU=0 Radius=8.8 StartAngle=1.29154 EndAngle=4.99164
    g2: LineSegment StartX=1.79164 StartY=6.2482 StartZ=0 EndX=2.42561 EndY=8.4591 EndZ=0
    g3: LineSegment StartX=1.79164 StartY=-6.2482 StartZ=0 EndX=2.42561 EndY=-8.4591 EndZ=0
    g4: ArcOfCircle CenterX=0 CenterY=0 CenterZ=0 NormalX=0 NormalY=0 NormalZ=1 AngleXU=0 Radius=6.5 StartAngle=4.99164 EndAngle=7.57473
    g5: ArcOfCircle CenterX=0 CenterY=0 CenterZ=0 NormalX=0 NormalY=0 NormalZ=1 AngleXU=0 Radius=12.5 StartAngle=0.567232 EndAngle=5.71595
    g6: LineSegment StartX=10.5424 StartY=6.71625 StartZ=0 EndX=7.25317 EndY=4.62078 EndZ=0
    g7: LineSegment StartX=10.5424 StartY=-6.71625 StartZ=0 EndX=7.25317 EndY=-4.62078 EndZ=0
    g8: ArcOfCircle CenterX=0 CenterY=0 CenterZ=0 NormalX=0 NormalY=0 NormalZ=1 AngleXU=0 Radius=8.6 StartAngle=5.71595 EndAngle=6.85042
    g9: GeomPoint X=15 Y=0 Z=0
    g10: LineSegment StartX=10.5424 StartY=6.71625 StartZ=0 EndX=15 EndY=0 EndZ=0
    g11: LineSegment StartX=15 StartY=0 StartZ=0 EndX=10.5424 EndY=-6.71625 EndZ=0
  constraints (31):
    c: Diameter(g0) = 12.2
    c: Coincident(g-1,g0)
    c: Coincident(g1,g-1)
    c: Diameter(g1) = 17.6
    c: Coincident(g2,g-4)
    c: PointOnObject(g-4,g2)
    c: Coincident(g2,g1)
    c: Coincident(g3,g-5)
    c: Coincident(g3,g1)
    c: PointOnObject(g-5,g3)
    c: Coincident(g4,g1)
    c: Coincident(g4,g2)
    c: Coincident(g4,g3)
    c: Coincident(g5,g1)
    c: Coincident(g6,g5)
    c: Coincident(g7,g5)
    c: Coincident(g8,g1)
    c: Coincident(g8,g7)
    c: Coincident(g8,g6)
    c: Perpendicular(g5,g6)
    c: Perpendicular(g8,g7)
    c: Diameter(g5) = 25
    c: Diameter(g8) = 17.2
    c: Angle(g7,g6) = 1.13446
    c: PointOnObject(g9,g-1)
    c: Coincident(g10,g5)
    c: Coincident(g10,g9)
    c: Coincident(g11,g9)
    c: Coincident(g11,g5)
    c: Equal(g11,g10)
    c: Distance(g9,g1) = 15
FEATURE [PartDesign::Pad] Pad023
  AllowMultiFace = false
  BaseFeature = -> Pad022
  Direction = (1,1,1)
  Length = 3.5
  Length2 = 100
  Profile = -> Sketch051
  Type = 0
  expr: Length = <<StockParts>>.AdapterBearingWidth
FEATURE [Sketcher::SketchObject] Sketch052
  ExternalGeometry = -> [Pad021]
  FullyConstrained = true
  MapMode = 5
  Placement = pos=(0,0,21.7) rot=(0,0,1;0rad)
  Support = -> [Pad023]
  expr: Constraints[0] = Sketch051.Constraints[0]
  expr: Constraints[23] = Sketch051.Constraints[23]
  expr: Constraints[32] = <<StockParts>>.AdapterBearingOuterDiameter - 2
  expr: Constraints[3] = Sketch051.Constraints[3]
  expr: Constraints[22] = Sketch051.Constraints[22]
  expr: Constraints[21] = Sketch051.Constraints[21]
  expr: Constraints[30] = Sketch051.Constraints[30]
  sketch-geometry (13):
    g0: Circle CenterX=0 CenterY=0 CenterZ=0 NormalX=0 NormalY=0 NormalZ=1 AngleXU=0 Radius=6.1
    g1: ArcOfCircle CenterX=0 CenterY=0 CenterZ=0 NormalX=0 NormalY=0 NormalZ=1 AngleXU=0 Radius=8.8 StartAngle=1.29154 EndAngle=4.99164
    g2: LineSegment StartX=1.79164 StartY=6.2482 StartZ=0 EndX=2.42561 EndY=8.4591 EndZ=0
    g3: LineSegment StartX=1.79164 StartY=-6.2482 StartZ=0 EndX=2.42561 EndY=-8.4591 EndZ=0
    g4: ArcOfCircle CenterX=0 CenterY=0 CenterZ=0 NormalX=0 NormalY=0 NormalZ=1 AngleXU=0 Radius=6.5 StartAngle=4.99164 EndAngle=7.57473
    g5: ArcOfCircle CenterX=0 CenterY=0 CenterZ=0 NormalX=0 NormalY=0 NormalZ=1 AngleXU=0 Radius=12.5 StartAngle=0.567232 EndAngle=5.71595
    g6: LineSegment StartX=10.5424 StartY=6.71625 StartZ=0 EndX=7.25317 EndY=4.62078 EndZ=0
    g7: LineSegment StartX=10.5424 StartY=-6.71625 StartZ=0 EndX=7.25317 EndY=-4.62078 EndZ=0
    g8: ArcOfCircle CenterX=0 CenterY=0 CenterZ=0 NormalX=0 NormalY=0 NormalZ=1 AngleXU=0 Radius=8.6 StartAngle=5.71595 EndAngle=6.85042
    g9: GeomPoint X=15 Y=0 Z=0
    g10: LineSegment StartX=10.5424 StartY=6.71625 StartZ=0 EndX=15 EndY=0 EndZ=0
    g11: LineSegment StartX=15 StartY=0 StartZ=0 EndX=10.5424 EndY=-6.71625 EndZ=0
    g12: Circle CenterX=0 CenterY=0 CenterZ=0 NormalX=0 NormalY=0 NormalZ=1 AngleXU=0 Radius=5
  constraints (33):
    c: Diameter(g0) = 12.2
    c: Coincident(g-1,g0)
    c: Coincident(g1,g-1)
    c: Diameter(g1) = 17.6
    c: Coincident(g2,g-4)
    c: PointOnObject(g-4,g2)
    c: Coincident(g2,g1)
    c: Coincident(g3,g-5)
    c: Coincident(g3,g1)
    c: PointOnObject(g-5,g3)
    c: Coincident(g4,g1)
    c: Coincident(g4,g2)
    c: Coincident(g4,g3)
    c: Coincident(g5,g1)
    c: Coincident(g6,g5)
    c: Coincident(g7,g5)
    c: Coincident(g8,g1)
    c: Coincident(g8,g7)
    c: Coincident(g8,g6)
    c: Perpendicular(g5,g6)
    c: Perpendicular(g8,g7)
    c: Diameter(g5) = 25
    c: Diameter(g8) = 17.2
    c: Angle(g7,g6) = 1.13446
    c: PointOnObject(g9,g-1)
    c: Coincident(g10,g5)
    c: Coincident(g10,g9)
    c: Coincident(g11,g9)
    c: Coincident(g11,g5)
    c: Equal(g11,g10)
    c: Distance(g9,g1) = 15
    c: Coincident(g12,g5)
    c: Diameter(g12) = 10
FEATURE [PartDesign::Pad] Pad024
  AllowMultiFace = false
  BaseFeature = -> Pad023
  Direction = (1,1,1)
  Length = 4
  Length2 = 100
  Profile = -> Sketch052
  Type = 0
FEATURE [PartDesign::Body] Body006  label="Cover Adapter"
  Group = -> [Sketch049,Pad021,Sketch050,Pad022,Sketch051,Pad023,Sketch052,Pad024]
  Origin = -> Origin007
  Placement = pos=(0,0,2.2) rot=(0,0,1;0rad)
  Tip = -> Pad024
FEATURE [Part::Feature] Solid
  shape: bbox 9.5 x 42 x 46 mm, 111 faces (baked)
FEATURE [Part::Feature] Solid001
  shape: bbox 9.2 x 42 x 42 mm, 47 faces (baked)
FEATURE [Part::Feature] Solid002
  shape: bbox 58 x 5 x 5 mm, 10 faces (baked)
FEATURE [Part::Feature] Solid003
  shape: bbox 3 x 15 x 15 mm, 12 faces (baked)
FEATURE [Part::Feature] Solid004
  shape: bbox 3 x 6.5 x 6.5 mm, 6 faces (baked)
FEATURE [Part::Feature] Solid005
  shape: bbox 3 x 15 x 15 mm, 12 faces (baked)
FEATURE [Part::Feature] Solid006
  shape: bbox 3 x 6.5 x 6.5 mm, 6 faces (baked)
FEATURE [Part::Feature] Solid007
  shape: bbox 5 x 15 x 10 mm, 27 faces (baked)
FEATURE [Part::Feature] Solid008 .. Solid013  x6 (patterned run collapsed; names and placements below)
  shape: bbox 0.5 x 0.5 x 3.5 mm, 8 faces (baked)
FEATURE [Part::Feature] Solid014
  shape: bbox 1.5 x 16 x 9 mm, 6 faces (baked)
FEATURE [Part::Feature] Solid015 .. Solid018  x4 (patterned run collapsed; names and placements below)
  shape: bbox 6.617 x 5.501 x 5.501 mm, 30 faces (baked)
FEATURE [Part::Feature] Solid019
  shape: bbox 21.9 x 41.92 x 41.92 mm, 18 faces (baked)
FEATURE [Part::Compound2] Compound  label="NEMA17"
  Links = -> [Solid,Solid001,Solid002,Solid003,Solid004,Solid005,Solid006,Solid007,Solid008,Solid009,Solid010,Solid011,Solid012,Solid013,Solid014,Solid015,Solid016,Solid017,Solid018,Solid019]
  Placement = pos=(-4.8e-15,-39,24) rot=(-0.707107,0,-0.707107;3.14159rad)
FEATURE [Part::FeaturePython] Screw  label="M3x16-Screw"  # Fasteners workbench fastener (typed FeaturePython)
  Placement = pos=(10.65,-32.65,0) rot=(1,0,0;3.14159rad)
  baseObject = -> Body [Edge17]
  diameter = 1
  invert = false
  length = 4
  lengthCustom = 16
  matchOuter = false
  offset = 0
  thread = false
  type = 21
FEATURE [Part::FeaturePython] Screw001  label="M3x16-Screw037"  # Fasteners workbench fastener (typed FeaturePython)
  Placement = pos=(10.65,-63.65,0) rot=(1,0,0;3.14159rad)
  baseObject = -> Body [Edge16]
  diameter = 1
  invert = false
  length = 4
  lengthCustom = 16
  matchOuter = false
  offset = 0
  thread = false
  type = 21
FEATURE [Part::FeaturePython] Screw002  label="M3x16-Screw038"  # Fasteners workbench fastener (typed FeaturePython)
  Placement = pos=(-20.35,-63.65,0) rot=(1,0,0;3.14159rad)
  baseObject = -> Body [Edge18]
  diameter = 1
  invert = false
  length = 4
  lengthCustom = 16
  matchOuter = false
  offset = 0
  thread = false
  type = 21
FEATURE [Part::FeaturePython] Screw003  label="M3x16-Screw039"  # Fasteners workbench fastener (typed FeaturePython)
  Placement = pos=(-20.35,-32.65,0) rot=(1,0,0;3.14159rad)
  baseObject = -> Body [Edge20]
  diameter = 1
  invert = false
  length = 4
  lengthCustom = 16
  matchOuter = false
  offset = 0
  thread = false
  type = 21
